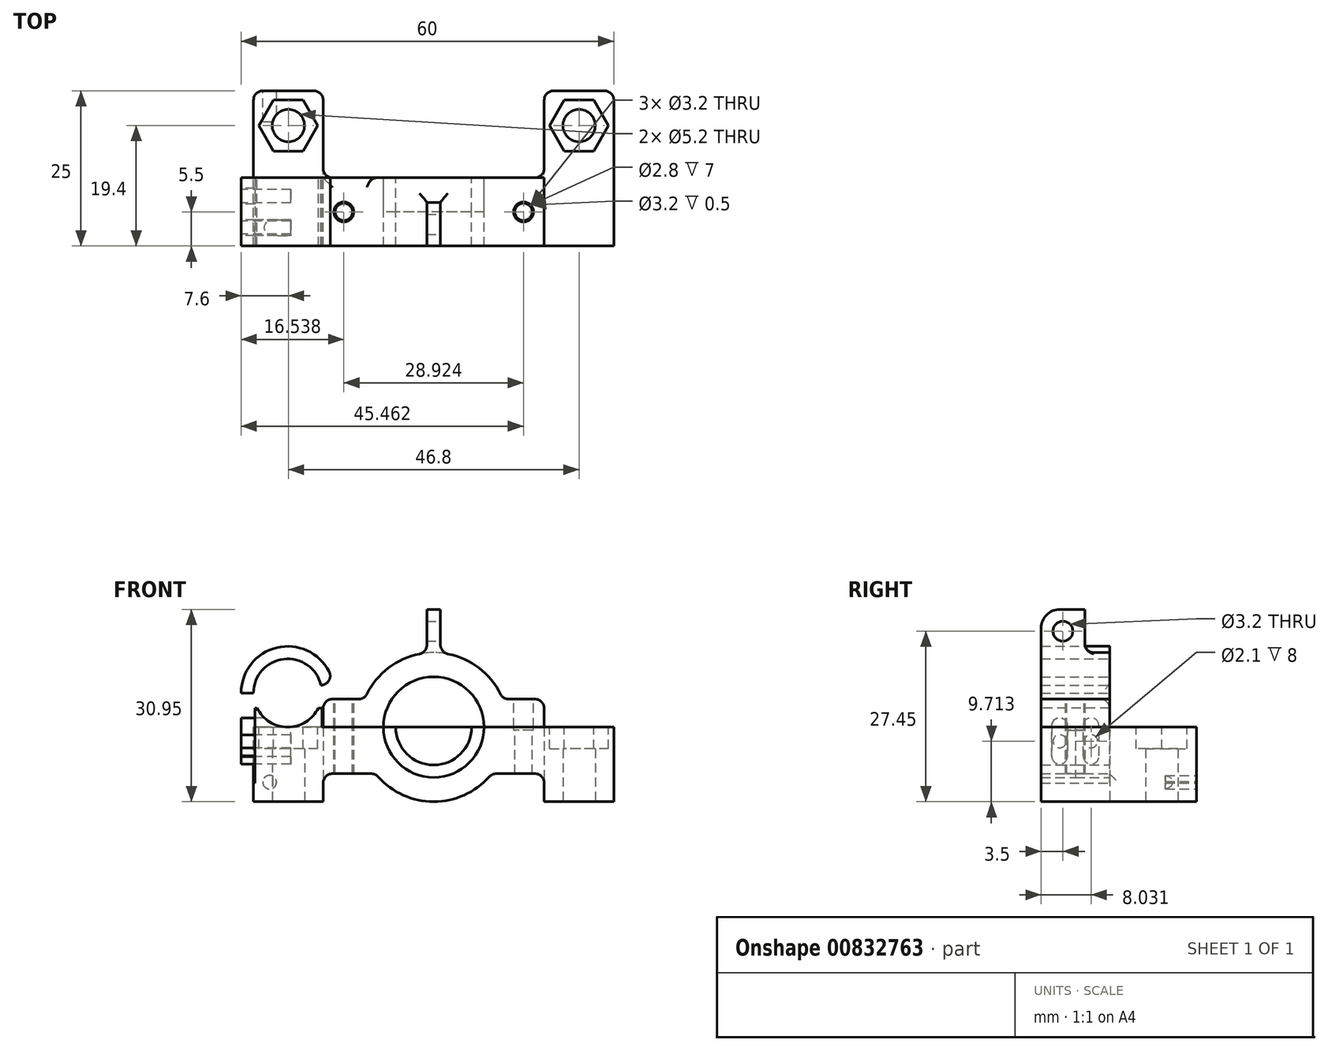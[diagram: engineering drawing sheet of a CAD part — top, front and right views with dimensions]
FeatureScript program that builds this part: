
annotation { "Feature Type Name" : "Feature", "Feature Type Description" : "" }
export const myFeature = defineFeature(function(context is Context, id is Id, definition is map)
    precondition{}
    {
        {
            var Q0;
            Q0=qCreatedBy(makeId("Top.planeOp"),FACE);
            var sketch = newSketch(context, id + "F0", { "sketchPlane" : qUnion([Q0])});
            skLineSegment(sketch, "E0", {"start": v(0, 15.09) * mm, "end": v(0, -18.84) * mm, "construction": true});
            skLineSegment(sketch, "E1", {"start": v(0, 0) * mm, "end": v(17.8, 0) * mm});
            skLineSegment(sketch, "E2", {"start": v(17.8, 0) * mm, "end": v(17.8, 14) * mm});
            skLineSegment(sketch, "E3", {"start": v(17.8, 14) * mm, "end": v(29, 14) * mm});
            skLineSegment(sketch, "E4", {"start": v(29, 14) * mm, "end": v(29, -11) * mm});
            skLineSegment(sketch, "E5", {"start": v(29, -11) * mm, "end": v(0, -11) * mm});
            skCircle(sketch, "E6", {"center": v(23.4, 8.4) * mm, "radius": 2.6 * mm});
            skLineSegment(sketch, "E7.MirrorCS", {"start": v(0, 0) * mm, "end": v(-17.8, 0) * mm});
            skLineSegment(sketch, "E8.MirrorCS", {"start": v(-17.8, 0) * mm, "end": v(-17.8, 14) * mm});
            skLineSegment(sketch, "E9.MirrorCS", {"start": v(-17.8, 14) * mm, "end": v(-29, 14) * mm});
            skLineSegment(sketch, "E10.MirrorCS", {"start": v(-29, 14) * mm, "end": v(-29, -11) * mm});
            skLineSegment(sketch, "E11.MirrorCS", {"start": v(-29, -11) * mm, "end": v(0, -11) * mm});
            skCircle(sketch, "E12.MirrorC", {"center": v(-23.4, 8.4) * mm, "radius": 2.6 * mm});
            skSolve(sketch);
        }
        {
            var Q0;
            Q0=makeQuery(id+"F0.imprint","IMPRINT",FACE,{"disambiguationData":[TD([[makeQuery(id+"F0.imprint","IMPRINT",EDGE,{"derivedFrom":sQuery(id+"F0.wireOp",EDGE,"E1")}),-1.0]])]});
            extrude(context, id + "F1", {"entities" : qUnion([Q0]), "depth" : 12 * mm, "offsetDistance" : 25 * mm});
        }
        {
            var Q0;
            Q0=makeQuery(id+"F1.opExtrude","SWEPT_FACE",FACE,{"disambiguationData":[OSD([sQuery(id+"F0.wireOp",EDGE,"E1"),sQuery(id+"F0.wireOp",EDGE,"E7.MirrorCS")])]});
            var sketch = newSketch(context, id + "F2", { "sketchPlane" : qUnion([Q0])});
            skLineSegment(sketch, "E13", {"start": v(0, -6.22) * mm, "end": v(0, 31.8) * mm, "construction": true});
            skCircle(sketch, "E14", {"center": v(0, 12) * mm, "radius": 6.1 * mm});
            skCircle(sketch, "E15", {"center": v(0, 12) * mm, "radius": 8.1 * mm});
            skCircle(sketch, "E16", {"center": v(0, 12) * mm, "radius": 12 * mm});
            skLineSegment(sketch, "E17", {"start": v(17.8, 4.5) * mm, "end": v(9.37, 4.5) * mm});
            skLineSegment(sketch, "E18", {"start": v(-9.37, 4.5) * mm, "end": v(-17.8, 4.5) * mm});
            skLineSegment(sketch, "E19", {"start": v(-17.8, 12) * mm, "end": v(-17.8, 16.5) * mm});
            skLineSegment(sketch, "E20", {"start": v(-17.8, 16.5) * mm, "end": v(-11.12, 16.5) * mm});
            skLineSegment(sketch, "E21.MirrorCS", {"start": v(17.8, 12) * mm, "end": v(17.8, 16.5) * mm});
            skLineSegment(sketch, "E22.MirrorCS", {"start": v(17.8, 16.5) * mm, "end": v(11.12, 16.5) * mm});
            skLineSegment(sketch, "E23", {"start": v(-1.1, 23.95) * mm, "end": v(-1.1, 30.95) * mm});
            skLineSegment(sketch, "E24", {"start": v(-1.1, 30.95) * mm, "end": v(0, 30.95) * mm});
            skLineSegment(sketch, "E25.MirrorCS", {"start": v(1.1, 23.95) * mm, "end": v(1.1, 30.95) * mm});
            skLineSegment(sketch, "E26.MirrorCS", {"start": v(1.1, 30.95) * mm, "end": v(0, 30.95) * mm});
            skArc(sketch, "E27", {"start": v(29, 17.5) * mm, "mid": v(24.13, 22.96) * mm, "end": v(18.14, 18.75) * mm});
            skArc(sketch, "E28", {"start": v(31, 17.5) * mm, "mid": v(24.13, 24.97) * mm, "end": v(16.1, 18.75) * mm});
            skLineSegment(sketch, "E29.0", {"start": v(29, 12) * mm, "end": v(29, 0) * mm});
            skLineSegment(sketch, "E30", {"start": v(29, 4.52) * mm, "end": v(29, 17.49) * mm});
            skLineSegment(sketch, "E31", {"start": v(31, 17.5) * mm, "end": v(31, 3) * mm});
            skLineSegment(sketch, "E32", {"start": v(31, 3) * mm, "end": v(29, 3) * mm});
            skLineSegment(sketch, "E33", {"start": v(18, 15.06) * mm, "end": v(18, 12) * mm});
            skLineSegment(sketch, "E34.0.0", {"start": v(17.8, 0) * mm, "end": v(29, 0) * mm});
            skLineSegment(sketch, "E34.0.1", {"start": v(29, 0) * mm, "end": v(29, 12) * mm});
            skLineSegment(sketch, "E34.0.2", {"start": v(29, 12) * mm, "end": v(17.8, 12) * mm});
            skLineSegment(sketch, "E34.0.3", {"start": v(17.8, 12) * mm, "end": v(17.8, 0) * mm});
            skPoint(sketch, "E35", {"position": v(16, 17.5) * mm});
            skPoint(sketch, "E36", {"position": v(29, 12) * mm});
            skLineSegment(sketch, "E37", {"start": v(29, 15.06) * mm, "end": v(28.43, 15.06) * mm});
            skLineSegment(sketch, "E38", {"start": v(18.57, 15.06) * mm, "end": v(18, 15.06) * mm});
            skArc(sketch, "E39.trimOffspring", {"start": v(18.57, 15.06) * mm, "mid": v(23.5, 12) * mm, "end": v(28.43, 15.06) * mm});
            skLineSegment(sketch, "E40", {"start": v(17.8, 12) * mm, "end": v(12.69, 12) * mm});
            skLineSegment(sketch, "E41", {"start": v(29, 17.5) * mm, "end": v(29, 3) * mm});
            skLineSegment(sketch, "E42", {"start": v(18.14, 18.75) * mm, "end": v(16.1, 18.75) * mm});
            skPoint(sketch, "E43.orphan", {"position": v(18, 17.5) * mm});
            skSolve(sketch);
        }
        {
            var Q0;
            {var subQ0=sQuery(id+"F2.wireOp",EDGE,"E17");Q0=makeQuery(id+"F2.imprint","IMPRINT",FACE,{"disambiguationData":[TD([[makeQuery(id+"F2.imprint","IMPRINT",EDGE,{"derivedFrom":subQ0}),1.0]])]});}
            var Q1;
            {var subQ0=sQuery(id+"F2.wireOp",EDGE,"E18");Q1=makeQuery(id+"F2.imprint","IMPRINT",FACE,{"disambiguationData":[TD([[makeQuery(id+"F2.imprint","IMPRINT",EDGE,{"derivedFrom":subQ0}),1.0]])]});}
            var Q2;
            {var subQ0=sQuery(id+"F2.wireOp",EDGE,"E14");var subQ1=makeQuery(id+"F1.opExtrude","CAP_EDGE",EDGE,{"disambiguationData":[OSD([sQuery(id+"F0.wireOp",EDGE,"E1"),sQuery(id+"F0.wireOp",EDGE,"E7.MirrorCS")])],"isStart":false});var subQ2=makeQuery(id+"F2.imprint","INTERSECT",VERTEX,{"disambiguationData":[OD(0.0)],"derivedFrom":[subQ1,subQ0]});Q2=makeQuery(id+"F2.imprint","IMPRINT",FACE,{"disambiguationData":[TD([[makeQuery(id+"F2.imprint","IMPRINT",EDGE,{"disambiguationData":[TD([[subQ2,1.0]])],"derivedFrom":subQ0}),1.0]])]});}
            extrude(context, id + "F3", {"entities" : qUnion([Q0, Q1, Q2]), "operationType" : NewBodyOperationType.REMOVE, "oppositeDirection" : true, "depth" : 25 * mm, "offsetDistance" : 25 * mm});
        }
        {
            var Q0;
            {var subQ5=sQuery(id+"F2.wireOp",EDGE,"E21.MirrorCS");Q0=makeQuery(id+"F2.imprint","IMPRINT",FACE,{"disambiguationData":[TD([[makeQuery(id+"F2.imprint","IMPRINT",EDGE,{"derivedFrom":subQ5}),1.0]])]});}
            var Q1;
            {var subQ0=sQuery(id+"F2.wireOp",EDGE,"E16");var subQ3=makeQuery(id+"F2.imprint","INTERSECT",VERTEX,{"derivedFrom":[subQ0,sQuery(id+"F2.wireOp",EDGE,"E22.MirrorCS")]});Q1=makeQuery(id+"F2.imprint","IMPRINT",FACE,{"disambiguationData":[TD([[makeQuery(id+"F2.imprint","IMPRINT",EDGE,{"disambiguationData":[TD([[subQ3,-1.0]])],"derivedFrom":subQ0}),1.0]])]});}
            var Q2;
            {var subQ0=sQuery(id+"F2.wireOp",EDGE,"E14");var subQ1=makeQuery(id+"F1.opExtrude","CAP_EDGE",EDGE,{"disambiguationData":[OSD([sQuery(id+"F0.wireOp",EDGE,"E1"),sQuery(id+"F0.wireOp",EDGE,"E7.MirrorCS")])],"isStart":false});var subQ2=makeQuery(id+"F2.imprint","INTERSECT",VERTEX,{"disambiguationData":[OD(0.0)],"derivedFrom":[subQ1,subQ0]});Q2=makeQuery(id+"F2.imprint","IMPRINT",FACE,{"disambiguationData":[TD([[makeQuery(id+"F2.imprint","IMPRINT",EDGE,{"disambiguationData":[TD([[subQ2,-1.0]])],"derivedFrom":subQ0}),-1.0]])]});}
            var Q3;
            {var subQ5=sQuery(id+"F2.wireOp",EDGE,"E19");Q3=makeQuery(id+"F2.imprint","IMPRINT",FACE,{"disambiguationData":[TD([[makeQuery(id+"F2.imprint","IMPRINT",EDGE,{"derivedFrom":subQ5}),-1.0]])]});}
            var Q4;
            {var subQ0=sQuery(id+"F2.wireOp",EDGE,"E23");Q4=makeQuery(id+"F2.imprint","IMPRINT",FACE,{"disambiguationData":[TD([[makeQuery(id+"F2.imprint","IMPRINT",EDGE,{"derivedFrom":subQ0}),-1.0]])]});}
            extrude(context, id + "F4", {"entities" : qUnion([Q0, Q1, Q2, Q3, Q4]), "oppositeDirection" : true, "depth" : 11 * mm, "offsetDistance" : 25 * mm});
        }
        {
            var Q0;
            {var subQ0=sQuery(id+"F2.wireOp",EDGE,"E14");var subQ1=makeQuery(id+"F1.opExtrude","CAP_EDGE",EDGE,{"disambiguationData":[OSD([sQuery(id+"F0.wireOp",EDGE,"E1"),sQuery(id+"F0.wireOp",EDGE,"E7.MirrorCS")])],"isStart":false});var subQ2=makeQuery(id+"F2.imprint","INTERSECT",VERTEX,{"disambiguationData":[OD(0.0)],"derivedFrom":[subQ1,subQ0]});Q0=makeQuery(id+"F2.imprint","IMPRINT",FACE,{"disambiguationData":[TD([[makeQuery(id+"F2.imprint","IMPRINT",EDGE,{"disambiguationData":[TD([[subQ2,1.0]])],"derivedFrom":subQ0}),-1.0]])]});}
            var Q1;
            {var subQ0=sQuery(id+"F2.wireOp",EDGE,"E14");var subQ1=makeQuery(id+"F1.opExtrude","CAP_EDGE",EDGE,{"disambiguationData":[OSD([sQuery(id+"F0.wireOp",EDGE,"E1"),sQuery(id+"F0.wireOp",EDGE,"E7.MirrorCS")])],"isStart":false});var subQ2=makeQuery(id+"F2.imprint","INTERSECT",VERTEX,{"disambiguationData":[OD(0.0)],"derivedFrom":[subQ1,subQ0]});Q1=makeQuery(id+"F2.imprint","IMPRINT",FACE,{"disambiguationData":[TD([[makeQuery(id+"F2.imprint","IMPRINT",EDGE,{"disambiguationData":[TD([[subQ2,-1.0]])],"derivedFrom":subQ0}),-1.0]])]});}
            extrude(context, id + "F5", {"entities" : qUnion([Q0, Q1]), "operationType" : NewBodyOperationType.REMOVE, "oppositeDirection" : true, "depth" : 5.5 * mm, "offsetDistance" : 25 * mm});
        }
        {
            var Q0;
            {var subQ1=sQuery(id+"F2.wireOp",EDGE,"E27");Q0=makeQuery(id+"F2.imprint","IMPRINT",FACE,{"disambiguationData":[TD([[makeQuery(id+"F2.imprint","IMPRINT",EDGE,{"derivedFrom":subQ1}),-1.0]])]});}
            extrude(context, id + "F6", {"entities" : qUnion([Q0]), "oppositeDirection" : true, "depth" : 11 * mm, "offsetDistance" : 25 * mm});
        }
        {
            var Q0;
            {var subQ3=sQuery(id+"F2.wireOp",EDGE,"E37");Q0=makeQuery(id+"F2.imprint","IMPRINT",FACE,{"disambiguationData":[TD([[makeQuery(id+"F2.imprint","IMPRINT",EDGE,{"derivedFrom":subQ3}),1.0]])]});}
            var Q1;
            {var subQ0=sQuery(id+"F2.wireOp",EDGE,"E33");Q1=makeQuery(id+"F2.imprint","IMPRINT",FACE,{"disambiguationData":[TD([[makeQuery(id+"F2.imprint","IMPRINT",EDGE,{"derivedFrom":subQ0}),1.0]])]});}
            extrude(context, id + "F7", {"entities" : qUnion([Q0, Q1]), "operationType" : NewBodyOperationType.ADD, "oppositeDirection" : true, "depth" : 11 * mm, "offsetDistance" : 25 * mm});
        }
        {
            var Q0;
            Q0=makeQuery(id+"F4.opExtrude","SWEPT_FACE",FACE,{"disambiguationData":[OSD([sQuery(id+"F2.wireOp",EDGE,"E20")])]});
            var sketch = newSketch(context, id + "F8", { "sketchPlane" : qUnion([Q0])});
            skCircle(sketch, "E44", {"center": v(14.46, -5.5) * mm, "radius": 1.6 * mm});
            skPoint(sketch, "E44.centerSnap0", {"position": v(14.46, 0) * mm});
            skPoint(sketch, "E44.centerSnap1", {"position": v(11.12, -5.5) * mm});
            skLineSegment(sketch, "E45", {"start": v(0, 0) * mm, "end": v(0, -11.05) * mm, "construction": true});
            skCircle(sketch, "E46.MirrorC", {"center": v(-14.46, -5.5) * mm, "radius": 1.6 * mm});
            skCircle(sketch, "E47", {"center": v(14.46, -5.5) * mm, "radius": 1.4 * mm});
            skCircle(sketch, "E48.MirrorC", {"center": v(-14.46, -5.5) * mm, "radius": 1.4 * mm});
            skSolve(sketch);
        }
        {
            var Q0;
            Q0=makeQuery(id+"F8.imprint","IMPRINT",FACE,{"disambiguationData":[TD([[makeQuery(id+"F8.imprint","IMPRINT",EDGE,{"derivedFrom":sQuery(id+"F8.wireOp",EDGE,"E47")}),1.0]])]});
            var Q1;
            Q1=makeQuery(id+"F8.imprint","IMPRINT",FACE,{"disambiguationData":[TD([[makeQuery(id+"F8.imprint","IMPRINT",EDGE,{"derivedFrom":sQuery(id+"F8.wireOp",EDGE,"E48.MirrorC")}),-1.0]])]});
            extrude(context, id + "F9", {"entities" : qUnion([Q0, Q1]), "operationType" : NewBodyOperationType.REMOVE, "oppositeDirection" : true, "depth" : 25 * mm, "offsetDistance" : 25 * mm});
        }
        {
            var Q0;
            Q0=makeQuery(id+"F8.imprint","IMPRINT",FACE,{"disambiguationData":[TD([[makeQuery(id+"F8.imprint","IMPRINT",EDGE,{"derivedFrom":sQuery(id+"F8.wireOp",EDGE,"E46.MirrorC")}),-1.0]])]});
            var Q1;
            Q1=makeQuery(id+"F8.imprint","IMPRINT",FACE,{"disambiguationData":[TD([[makeQuery(id+"F8.imprint","IMPRINT",EDGE,{"derivedFrom":sQuery(id+"F8.wireOp",EDGE,"E44")}),1.0]])]});
            extrude(context, id + "F10", {"entities" : qUnion([Q0, Q1]), "operationType" : NewBodyOperationType.REMOVE, "oppositeDirection" : true, "depth" : 5 * mm, "offsetDistance" : 25 * mm});
        }
        {
            var Q0;
            Q0=makeQuery(id+"F6.opExtrude","SWEPT_FACE",FACE,{"disambiguationData":[OSD([sQuery(id+"F2.wireOp",EDGE,"E31")])]});
            var sketch = newSketch(context, id + "F11", { "sketchPlane" : qUnion([Q0])});
            skLineSegment(sketch, "E49", {"start": v(4.23, 9.71) * mm, "end": v(4.23, 9.71) * mm});
            skPoint(sketch, "E50.0", {"position": v(5.5, 16.5) * mm});
            skLineSegment(sketch, "E51", {"start": v(5.5, 16.5) * mm, "end": v(5.5, 3) * mm, "construction": true});
            skLineSegment(sketch, "E52.MirrorC", {"start": v(6.77, 9.71) * mm, "end": v(6.77, 9.71) * mm});
            skLineSegment(sketch, "E53", {"start": v(2.97, 10.97) * mm, "end": v(8.6, 10.97) * mm, "construction": true});
            skArc(sketch, "E54.MirrorC", {"start": v(1.7, 12.23) * mm, "mid": v(2.97, 13.5) * mm, "end": v(4.23, 12.23) * mm});
            skArc(sketch, "E55.MirrorC", {"start": v(9.3, 12.23) * mm, "mid": v(8.03, 13.5) * mm, "end": v(6.77, 12.23) * mm});
            skLineSegment(sketch, "E56", {"start": v(1.7, 9.71) * mm, "end": v(1.7, 12.23) * mm});
            skLineSegment(sketch, "E57", {"start": v(4.23, 9.71) * mm, "end": v(4.23, 12.23) * mm});
            skLineSegment(sketch, "E58.MirrorCS", {"start": v(6.77, 9.71) * mm, "end": v(6.77, 12.23) * mm});
            skLineSegment(sketch, "E59.MirrorCS", {"start": v(9.3, 9.71) * mm, "end": v(9.3, 12.23) * mm});
            skCircle(sketch, "E60", {"center": v(2.97, 9.71) * mm, "radius": 1.05 * mm});
            skCircle(sketch, "E61.MirrorC", {"center": v(8.03, 9.71) * mm, "radius": 1.05 * mm});
            skLineSegment(sketch, "E62", {"start": v(9.29, 7.24) * mm, "end": v(9.3, 9.71) * mm});
            skLineSegment(sketch, "E63", {"start": v(6.77, 7.24) * mm, "end": v(6.77, 9.71) * mm});
            skArc(sketch, "E64.trimOffspring", {"start": v(6.77, 7.38) * mm, "mid": v(8.03, 6.05) * mm, "end": v(9.29, 7.38) * mm});
            skLineSegment(sketch, "E65.MirrorCS", {"start": v(1.71, 7.24) * mm, "end": v(1.7, 9.71) * mm});
            skArc(sketch, "E66.MirrorCS", {"start": v(4.23, 7.38) * mm, "mid": v(2.97, 6.05) * mm, "end": v(1.71, 7.38) * mm});
            skLineSegment(sketch, "E67.MirrorCS", {"start": v(4.23, 7.24) * mm, "end": v(4.23, 9.71) * mm});
            skSolve(sketch);
        }
        {
            var Q0;
            Q0=makeQuery(id+"F11.imprint","IMPRINT",FACE,{"disambiguationData":[TD([[makeQuery(id+"F11.imprint","IMPRINT",EDGE,{"derivedFrom":sQuery(id+"F11.wireOp",EDGE,"E61.MirrorC")}),-1.0]])]});
            var Q1;
            Q1=makeQuery(id+"F11.imprint","IMPRINT",FACE,{"disambiguationData":[TD([[makeQuery(id+"F11.imprint","IMPRINT",EDGE,{"derivedFrom":sQuery(id+"F11.wireOp",EDGE,"E60")}),1.0]])]});
            extrude(context, id + "F12", {"entities" : qUnion([Q0, Q1]), "operationType" : NewBodyOperationType.REMOVE, "oppositeDirection" : true, "depth" : 8 * mm, "offsetDistance" : 25 * mm});
        }
        {
            var Q0;
            Q0=makeQuery(id+"F11.imprint","IMPRINT",FACE,{"disambiguationData":[TD([[makeQuery(id+"F11.imprint","IMPRINT",EDGE,{"derivedFrom":sQuery(id+"F11.wireOp",EDGE,"E55.MirrorC")}),1.0]])]});
            var Q1;
            Q1=makeQuery(id+"F11.imprint","IMPRINT",FACE,{"disambiguationData":[TD([[makeQuery(id+"F11.imprint","IMPRINT",EDGE,{"derivedFrom":sQuery(id+"F11.wireOp",EDGE,"E54.MirrorC")}),-1.0]])]});
            extrude(context, id + "F13", {"entities" : qUnion([Q0, Q1]), "operationType" : NewBodyOperationType.REMOVE, "oppositeDirection" : true, "depth" : 2.2 * mm, "offsetDistance" : 25 * mm});
        }
        {
            var Q0;
            {var subQ0=sQuery(id+"F2.wireOp",EDGE,"E23");Q0=makeQuery(id+"F2.imprint","IMPRINT",FACE,{"disambiguationData":[TD([[makeQuery(id+"F2.imprint","IMPRINT",EDGE,{"derivedFrom":subQ0}),-1.0]])]});}
            var sketch = newSketch(context, id + "F14", { "sketchPlane" : qUnion([Q0])});
            skPoint(sketch, "E68.0", {"position": v(1.1, 23.95) * mm});
            skPoint(sketch, "E69.0", {"position": v(-1.1, 23.95) * mm});
            skLineSegment(sketch, "E70", {"start": v(1.1, 23.95) * mm, "end": v(-1.1, 23.95) * mm});
            skSolve(sketch);
        }
        {
            var Q0;
            Q0 = qSketchRegion(id + "F14", true);
            var Q1;
            {var subQ0=sQuery(id+"F2.wireOp",EDGE,"E23");Q1=makeQuery(id+"F2.imprint","IMPRINT",FACE,{"disambiguationData":[TD([[makeQuery(id+"F2.imprint","IMPRINT",EDGE,{"derivedFrom":subQ0}),-1.0]])]});}
            extrude(context, id + "F15", {"entities" : qUnion([Q0, Q1]), "operationType" : NewBodyOperationType.REMOVE, "oppositeDirection" : true, "depth" : 4 * mm, "offsetDistance" : 25 * mm});
        }
        {
            var Q0;
            Q0=makeQuery(id+"F4.opExtrude","SWEPT_FACE",FACE,{"disambiguationData":[OSD([sQuery(id+"F2.wireOp",EDGE,"E23")])]});
            var sketch = newSketch(context, id + "F16", { "sketchPlane" : qUnion([Q0])});
            skCircle(sketch, "E71", {"center": v(-7.5, 27.45) * mm, "radius": 1.6 * mm});
            skPoint(sketch, "E71.centerSnap0", {"position": v(-7.5, 30.95) * mm});
            skPoint(sketch, "E71.centerSnap1", {"position": v(-11, 27.45) * mm});
            skSolve(sketch);
        }
        {
            var Q0;
            Q0=makeQuery(id+"F16.imprint","IMPRINT",FACE,{"disambiguationData":[TD([[makeQuery(id+"F16.imprint","IMPRINT",EDGE,{"derivedFrom":sQuery(id+"F16.wireOp",EDGE,"E71")}),1.0]])]});
            extrude(context, id + "F17", {"entities" : qUnion([Q0]), "operationType" : NewBodyOperationType.REMOVE, "oppositeDirection" : true, "depth" : 3 * mm, "offsetDistance" : 25 * mm});
        }
        {
            var Q0;
            Q0=makeQuery(id+"F4.opExtrude","SWEPT_EDGE",EDGE,{"disambiguationData":[OSD([sQuery(id+"F2.wireOp",EDGE,"E16"),sQuery(id+"F2.wireOp",EDGE,"E22.MirrorCS")])]});
            var Q1;
            Q1=makeQuery(id+"F4.opExtrude","SWEPT_EDGE",EDGE,{"disambiguationData":[OSD([sQuery(id+"F2.wireOp",EDGE,"E16"),sQuery(id+"F2.wireOp",EDGE,"E20")])]});
            var Q2;
            Q2=makeQuery(id+"F4.opExtrude","SWEPT_EDGE",EDGE,{"disambiguationData":[OSD([sQuery(id+"F2.wireOp",EDGE,"E16"),sQuery(id+"F2.wireOp",EDGE,"E23")])]});
            var Q3;
            Q3=makeQuery(id+"F4.opExtrude","SWEPT_EDGE",EDGE,{"disambiguationData":[OSD([sQuery(id+"F2.wireOp",EDGE,"E16"),sQuery(id+"F2.wireOp",EDGE,"E25.MirrorCS")])]});
            var Q4;
            Q4=makeQuery(id+"F15.boolean.opBoolean","COPY",EDGE,{"derivedFrom":makeQuery(id+"F15.opExtrude","CAP_EDGE",EDGE,{"disambiguationData":[OSD([sQuery(id+"F2.wireOp",EDGE,"E16")])],"isStart":false})});
            var Q5;
            Q5=makeQuery(id+"F4.opExtrude","CAP_EDGE",EDGE,{"disambiguationData":[OSD([sQuery(id+"F2.wireOp",EDGE,"E22.MirrorCS")])],"isStart":true});
            var Q6;
            Q6=makeQuery(id+"F4.opExtrude","SWEPT_EDGE",EDGE,{"disambiguationData":[OSD([sQuery(id+"F2.wireOp",EDGE,"E19"),sQuery(id+"F2.wireOp",EDGE,"E20")])]});
            var Q7;
            Q7=makeQuery(id+"F4.opExtrude","SWEPT_EDGE",EDGE,{"disambiguationData":[OSD([sQuery(id+"F2.wireOp",EDGE,"E21.MirrorCS"),sQuery(id+"F2.wireOp",EDGE,"E22.MirrorCS")])]});
            fillet(context, id + "F18", {"entities" : qUnion([Q0, Q1, Q2, Q3, Q4, Q5, Q6, Q7]), "radius" : 1.5 * mm, "tangentPropagation" : true, "allowEdgeOverflow" : false});
        }
        {
            var Q0;
            Q0=makeQuery(id+"F15.boolean.opBoolean","COPY",EDGE,{"derivedFrom":makeQuery(id+"F15.opExtrude","CAP_EDGE",EDGE,{"disambiguationData":[OSD([sQuery(id+"F2.wireOp",EDGE,"E24"),sQuery(id+"F2.wireOp",EDGE,"E26.MirrorCS")])],"isStart":false})});
            var Q1;
            Q1=makeQuery(id+"F4.opExtrude","CAP_EDGE",EDGE,{"disambiguationData":[OSD([sQuery(id+"F2.wireOp",EDGE,"E24"),sQuery(id+"F2.wireOp",EDGE,"E26.MirrorCS")])],"isStart":false});
            fillet(context, id + "F19", {"entities" : qUnion([Q0, Q1]), "radius" : 3 * mm, "tangentPropagation" : true, "allowEdgeOverflow" : false});
        }
        {
            var Q0;
            {var subQ0=sQuery(id+"F0.wireOp",EDGE,"E4");var subQ1=sQuery(id+"F0.wireOp",EDGE,"E3");var subQ2=sQuery(id+"F0.wireOp",EDGE,"E2");var subQ3=sQuery(id+"F0.wireOp",EDGE,"E7.MirrorCS");var subQ4=sQuery(id+"F0.wireOp",EDGE,"E1");var subQ5=sQuery(id+"F0.wireOp",EDGE,"E11.MirrorCS");var subQ6=sQuery(id+"F0.wireOp",EDGE,"E5");var subQ7=sQuery(id+"F0.wireOp",EDGE,"E6");Q0=makeQuery(id+"F3.boolean.opBoolean","SPLIT",FACE,{"disambiguationData":[TD([makeQuery(id+"F1.opExtrude","SWEPT_FACE",FACE,{"disambiguationData":[OSD([subQ2])]})])],"derivedFrom":makeQuery(id+"F1.opExtrude","CAP_FACE",FACE,{"disambiguationData":[OSD([subQ4,subQ2,subQ1,subQ0,subQ6,subQ7,subQ3,sQuery(id+"F0.wireOp",EDGE,"E8.MirrorCS"),sQuery(id+"F0.wireOp",EDGE,"E9.MirrorCS"),sQuery(id+"F0.wireOp",EDGE,"E10.MirrorCS"),subQ5,sQuery(id+"F0.wireOp",EDGE,"E12.MirrorC")])],"isStart":false})});}
            var sketch = newSketch(context, id + "F20", { "sketchPlane" : qUnion([Q0])});
            skCircle(sketch, "E72.cCircle", {"center": v(23.4, 8.4) * mm, "radius": 4.1 * mm, "construction": true});
            skLineSegment(sketch, "E72.0", {"start": v(25.77, 4.3) * mm, "end": v(21.03, 4.3) * mm});
            skLineSegment(sketch, "E72.1", {"start": v(21.03, 4.3) * mm, "end": v(18.67, 8.4) * mm});
            skLineSegment(sketch, "E72.2", {"start": v(18.67, 8.4) * mm, "end": v(21.03, 12.5) * mm});
            skLineSegment(sketch, "E72.3", {"start": v(21.03, 12.5) * mm, "end": v(25.77, 12.5) * mm});
            skLineSegment(sketch, "E72.4", {"start": v(25.77, 12.5) * mm, "end": v(28.13, 8.4) * mm});
            skLineSegment(sketch, "E72.5", {"start": v(28.13, 8.4) * mm, "end": v(25.77, 4.3) * mm});
            skPoint(sketch, "E72.0.midPoint", {"position": v(23.4, 4.3) * mm});
            skLineSegment(sketch, "E73.MirrorCS", {"start": v(-21.03, 12.5) * mm, "end": v(-25.77, 12.5) * mm});
            skLineSegment(sketch, "E74.MirrorCS", {"start": v(-25.77, 12.5) * mm, "end": v(-28.13, 8.4) * mm});
            skLineSegment(sketch, "E75.MirrorCS", {"start": v(-28.13, 8.4) * mm, "end": v(-25.77, 4.3) * mm});
            skLineSegment(sketch, "E76.MirrorCS", {"start": v(-25.77, 4.3) * mm, "end": v(-21.03, 4.3) * mm});
            skLineSegment(sketch, "E77.MirrorCS", {"start": v(-21.03, 4.3) * mm, "end": v(-18.67, 8.4) * mm});
            skLineSegment(sketch, "E78.MirrorCS", {"start": v(-18.67, 8.4) * mm, "end": v(-21.03, 12.5) * mm});
            skSolve(sketch);
        }
        {
            var Q0;
            Q0=makeQuery(id+"F20.imprint","IMPRINT",FACE,{"disambiguationData":[TD([[makeQuery(id+"F20.imprint","IMPRINT",EDGE,{"derivedFrom":sQuery(id+"F20.wireOp",EDGE,"E72.0")}),-1.0]])]});
            var Q1;
            Q1=makeQuery(id+"F20.imprint","IMPRINT",FACE,{"disambiguationData":[TD([[makeQuery(id+"F20.imprint","IMPRINT",EDGE,{"derivedFrom":sQuery(id+"F20.wireOp",EDGE,"E73.MirrorCS")}),1.0]])]});
            extrude(context, id + "F21", {"entities" : qUnion([Q0, Q1]), "operationType" : NewBodyOperationType.REMOVE, "oppositeDirection" : true, "depth" : 3.5 * mm, "offsetDistance" : 25 * mm});
        }
        {
            var Q0;
            Q0=makeQuery(id+"F1.opExtrude","SWEPT_EDGE",EDGE,{"disambiguationData":[OSD([sQuery(id+"F0.wireOp",EDGE,"E9.MirrorCS"),sQuery(id+"F0.wireOp",EDGE,"E10.MirrorCS")])]});
            var Q1;
            Q1=makeQuery(id+"F1.opExtrude","SWEPT_EDGE",EDGE,{"disambiguationData":[OSD([sQuery(id+"F0.wireOp",EDGE,"E8.MirrorCS"),sQuery(id+"F0.wireOp",EDGE,"E9.MirrorCS")])]});
            var Q2;
            Q2=makeQuery(id+"F1.opExtrude","SWEPT_EDGE",EDGE,{"disambiguationData":[OSD([sQuery(id+"F0.wireOp",EDGE,"E2"),sQuery(id+"F0.wireOp",EDGE,"E3")])]});
            var Q3;
            Q3=makeQuery(id+"F1.opExtrude","SWEPT_EDGE",EDGE,{"disambiguationData":[OSD([sQuery(id+"F0.wireOp",EDGE,"E3"),sQuery(id+"F0.wireOp",EDGE,"E4")])]});
            fillet(context, id + "F22", {"entities" : qUnion([Q0, Q1, Q2, Q3]), "radius" : 1.5 * mm, "tangentPropagation" : true, "allowEdgeOverflow" : false});
        }
        {
            var Q0;
            Q0=makeQuery(id+"F1.opExtrude","SWEPT_FACE",FACE,{"disambiguationData":[OSD([sQuery(id+"F0.wireOp",EDGE,"E9.MirrorCS")])]});
            var sketch = newSketch(context, id + "F23", { "sketchPlane" : qUnion([Q0])});
            skCircle(sketch, "E79", {"center": v(26.4, 3.13) * mm, "radius": 1.1 * mm});
            skSolve(sketch);
        }
        {
            var Q0;
            {var subQ0=sQuery(id+"F23.wireOp",EDGE,"E79");var subQ1=sQuery(id+"F0.wireOp",EDGE,"E9.MirrorCS");var subQ2=makeQuery(id+"F22.opFillet","BLEND_EDGE",EDGE,{"blendedFrom":[makeQuery(id+"F1.opExtrude","SWEPT_EDGE",EDGE,{"disambiguationData":[OSD([subQ1,sQuery(id+"F0.wireOp",EDGE,"E10.MirrorCS")])]}),makeQuery(id+"F1.opExtrude","SWEPT_FACE",FACE,{"disambiguationData":[OSD([subQ1])]})],"blendedInto":[makeQuery(id+"F1.opExtrude","SWEPT_FACE",FACE,{"disambiguationData":[OSD([subQ1])]})]});var subQ3=makeQuery(id+"F23.imprint","INTERSECT",VERTEX,{"disambiguationData":[OD(0.0)],"derivedFrom":[subQ2,subQ0]});Q0=makeQuery(id+"F23.imprint","IMPRINT",FACE,{"disambiguationData":[TD([[makeQuery(id+"F23.imprint","IMPRINT",EDGE,{"disambiguationData":[TD([[subQ3,1.0]])],"derivedFrom":subQ0}),1.0]])]});}
            extrude(context, id + "F24", {"entities" : qUnion([Q0]), "operationType" : NewBodyOperationType.REMOVE, "oppositeDirection" : true, "depth" : 5 * mm, "offsetDistance" : 25 * mm});
        }
        {
            var Q0;
            Q0=makeQuery(id+"F6.opExtrude","SWEPT_EDGE",EDGE,{"disambiguationData":[OSD([sQuery(id+"F2.wireOp",EDGE,"E28"),sQuery(id+"F2.wireOp",EDGE,"E42")])]});
            var Q1;
            Q1=makeQuery(id+"F6.opExtrude","SWEPT_EDGE",EDGE,{"disambiguationData":[OSD([sQuery(id+"F2.wireOp",EDGE,"E31"),sQuery(id+"F2.wireOp",EDGE,"E32")])]});
            fillet(context, id + "F25", {"entities" : qUnion([Q0, Q1]), "radius" : 1.5 * mm, "tangentPropagation" : true, "allowEdgeOverflow" : false});
        }
        {
            var Q0;
            Q0=makeQuery(id+"F1.opExtrude","SWEPT_EDGE",EDGE,{"disambiguationData":[OSD([sQuery(id+"F0.wireOp",EDGE,"E7.MirrorCS"),sQuery(id+"F0.wireOp",EDGE,"E8.MirrorCS")])]});
            var Q1;
            Q1=makeQuery(id+"F1.opExtrude","SWEPT_EDGE",EDGE,{"disambiguationData":[OSD([sQuery(id+"F0.wireOp",EDGE,"E1"),sQuery(id+"F0.wireOp",EDGE,"E2")])]});
            var Q2;
            Q2=makeQuery(id+"F3.boolean.opBoolean","COPY",EDGE,{"derivedFrom":makeQuery(id+"F3.opExtrude","SWEPT_EDGE",EDGE,{"disambiguationData":[OSD([sQuery(id+"F2.wireOp",EDGE,"E17"),sQuery(id+"F2.wireOp",EDGE,"E34.0.3")])]})});
            var Q3;
            Q3=makeQuery(id+"F3.boolean.opBoolean","COPY",EDGE,{"derivedFrom":makeQuery(id+"F3.opExtrude","SWEPT_EDGE",EDGE,{"disambiguationData":[OSD([sQuery(id+"F2.wireOp",EDGE,"E16"),sQuery(id+"F2.wireOp",EDGE,"E17")])]})});
            var Q4;
            Q4=makeQuery(id+"F3.boolean.opBoolean","COPY",EDGE,{"derivedFrom":makeQuery(id+"F3.opExtrude","SWEPT_EDGE",EDGE,{"disambiguationData":[OSD([sQuery(id+"F2.wireOp",EDGE,"E16"),sQuery(id+"F2.wireOp",EDGE,"E18")])]})});
            var Q5;
            Q5=makeQuery(id+"F3.boolean.opBoolean","COPY",EDGE,{"derivedFrom":makeQuery(id+"F3.opExtrude","SWEPT_EDGE",EDGE,{"disambiguationData":[OSD([sQuery(id+"F0.wireOp",EDGE,"E1"),sQuery(id+"F0.wireOp",EDGE,"E2"),sQuery(id+"F2.wireOp",EDGE,"E18")])]})});
            var Q6;
            Q6=makeQuery(id+"F3.boolean.opBoolean","COPY",EDGE,{"derivedFrom":makeQuery(id+"F3.opExtrude","CAP_EDGE",EDGE,{"disambiguationData":[OSD([sQuery(id+"F2.wireOp",EDGE,"E17")])],"isStart":true})});
            fillet(context, id + "F26", {"entities" : qUnion([Q0, Q1, Q2, Q3, Q4, Q5, Q6]), "radius" : 1.5 * mm, "tangentPropagation" : true, "allowEdgeOverflow" : false});
        }
    });
